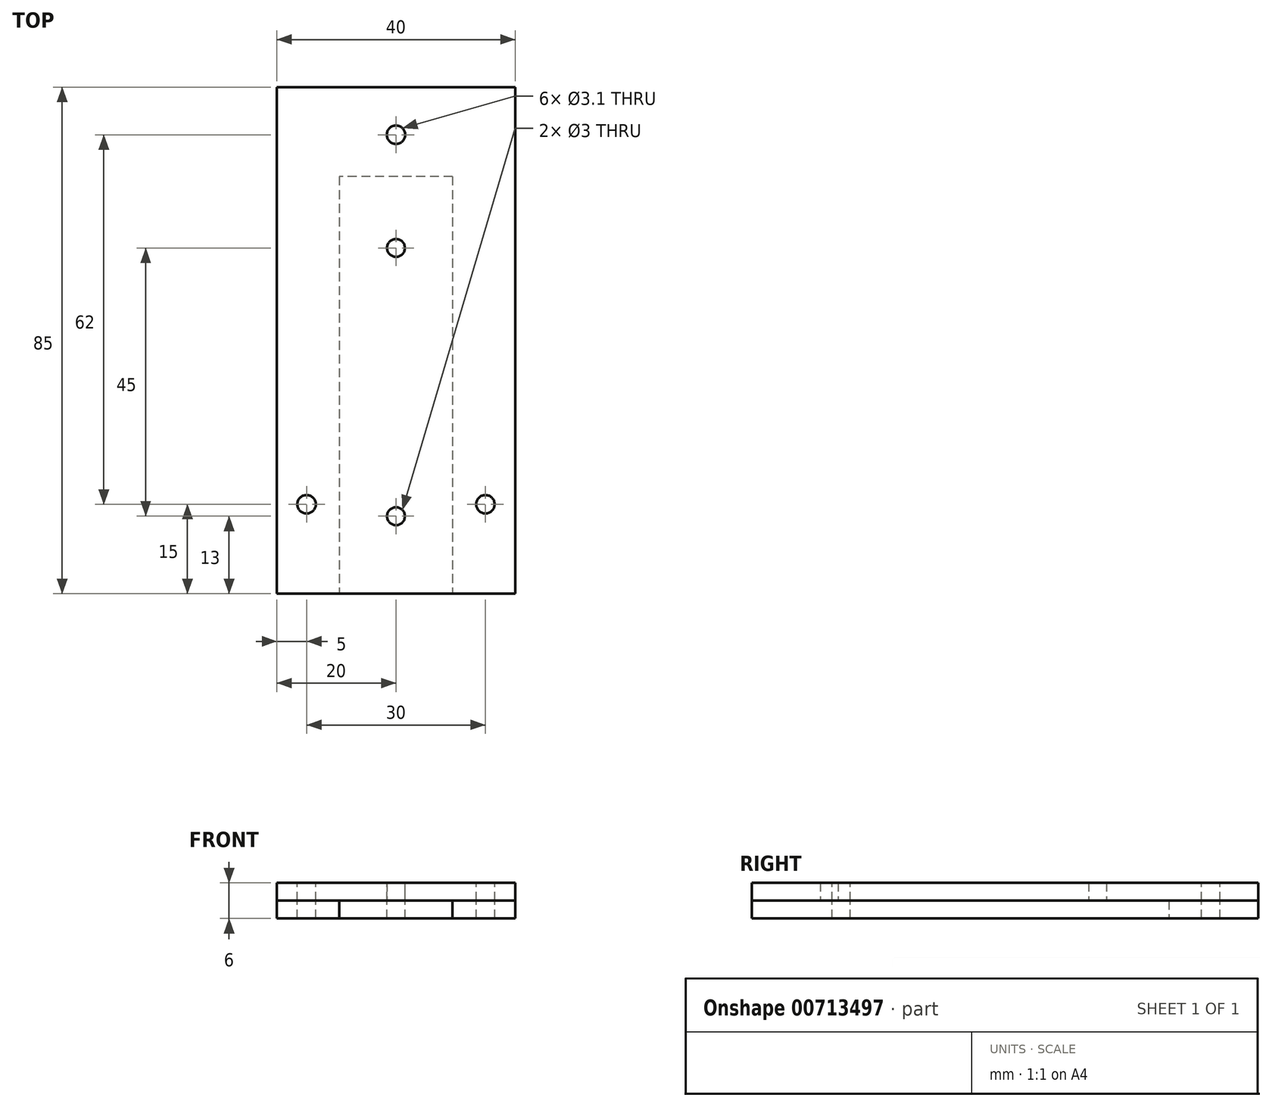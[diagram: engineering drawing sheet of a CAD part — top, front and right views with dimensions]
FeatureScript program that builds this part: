
annotation { "Feature Type Name" : "Feature", "Feature Type Description" : "" }
export const myFeature = defineFeature(function(context is Context, id is Id, definition is map)
    precondition{}
    {
        {
            var Q0;
            Q0=qCreatedBy(makeId("Top.planeOp"),FACE);
            var sketch = newSketch(context, id + "F0", { "sketchPlane" : qUnion([Q0])});
            skLineSegment(sketch, "E0.bottom", {"start": v(9.5, 35) * mm, "end": v(-9.5, 35) * mm});
            skLineSegment(sketch, "E0.top", {"start": v(9.5, -35) * mm, "end": v(-9.5, -35) * mm});
            skLineSegment(sketch, "E0.left", {"start": v(9.5, 35) * mm, "end": v(9.5, -35) * mm});
            skLineSegment(sketch, "E0.right", {"start": v(-9.5, 35) * mm, "end": v(-9.5, -35) * mm});
            skPoint(sketch, "E0.middle", {"position": v(0, 0) * mm});
            skLineSegment(sketch, "E1.bottom", {"start": v(20, 50) * mm, "end": v(-20, 50) * mm});
            skLineSegment(sketch, "E1.top", {"start": v(20, -50) * mm, "end": v(-20, -50) * mm});
            skLineSegment(sketch, "E1.left", {"start": v(20, 50) * mm, "end": v(20, -50) * mm});
            skLineSegment(sketch, "E1.right", {"start": v(-20, 50) * mm, "end": v(-20, -50) * mm});
            skLineSegment(sketch, "E2", {"start": v(-20, -35) * mm, "end": v(21.12, -35) * mm});
            skSolve(sketch);
        }
        {
            var Q0;
            Q0=makeQuery(id+"F0.imprint","IMPRINT",FACE,{"disambiguationData":[TD([[makeQuery(id+"F0.imprint","IMPRINT",EDGE,{"derivedFrom":sQuery(id+"F0.wireOp",EDGE,"E0.bottom")}),-1.0]])]});
            extrude(context, id + "F1", {"entities" : qUnion([Q0]), "depth" : 3 * mm, "offsetDistance" : 25 * mm});
        }
        {
            var Q0;
            Q0=makeQuery(id+"F1.opExtrude","CAP_FACE",FACE,{"disambiguationData":[OSD([sQuery(id+"F0.wireOp",EDGE,"E0.bottom"),sQuery(id+"F0.wireOp",EDGE,"E0.left"),sQuery(id+"F0.wireOp",EDGE,"E0.right"),sQuery(id+"F0.wireOp",EDGE,"E1.bottom"),sQuery(id+"F0.wireOp",EDGE,"E1.left"),sQuery(id+"F0.wireOp",EDGE,"E1.right"),sQuery(id+"F0.wireOp",EDGE,"E2")])],"isStart":false});
            var sketch = newSketch(context, id + "F2", { "sketchPlane" : qUnion([Q0])});
            skLineSegment(sketch, "E3.bottom", {"start": v(20, 50) * mm, "end": v(-20, 50) * mm});
            skLineSegment(sketch, "E3.top", {"start": v(20, -50) * mm, "end": v(-20, -50) * mm});
            skLineSegment(sketch, "E3.left", {"start": v(20, 50) * mm, "end": v(20, -50) * mm});
            skLineSegment(sketch, "E3.right", {"start": v(-20, 50) * mm, "end": v(-20, -50) * mm});
            skPoint(sketch, "E3.middle", {"position": v(0, 0) * mm});
            skLineSegment(sketch, "E4", {"start": v(-20, -35) * mm, "end": v(20, -35) * mm});
            skSolve(sketch);
        }
        {
            var Q0;
            {var subQ4=sQuery(id+"F2.wireOp",EDGE,"E3.bottom");Q0=makeQuery(id+"F2.imprint","IMPRINT",FACE,{"disambiguationData":[TD([[makeQuery(id+"F2.imprint","IMPRINT",EDGE,{"derivedFrom":subQ4}),1.0]])]});}
            var Q1;
            Q1=makeQuery(id+"F2.imprint","IMPRINT",FACE,{"disambiguationData":[TD([[makeQuery(id+"F2.imprint","IMPRINT",EDGE,{"derivedFrom":makeQuery(id+"F1.opExtrude","CAP_EDGE",EDGE,{"disambiguationData":[OSD([sQuery(id+"F0.wireOp",EDGE,"E0.bottom")])],"isStart":false})}),1.0]])]});
            extrude(context, id + "F3", {"entities" : qUnion([Q0, Q1]), "depth" : 3 * mm, "offsetDistance" : 25 * mm});
        }
        {
            var Q0;
            Q0=makeQuery(id+"F3.opExtrude","CAP_FACE",FACE,{"disambiguationData":[OSD([sQuery(id+"F2.wireOp",EDGE,"E3.bottom"),sQuery(id+"F2.wireOp",EDGE,"E3.left"),sQuery(id+"F2.wireOp",EDGE,"E3.right"),sQuery(id+"F2.wireOp",EDGE,"E4")])],"isStart":false});
            var sketch = newSketch(context, id + "F4", { "sketchPlane" : qUnion([Q0])});
            skCircle(sketch, "E5", {"center": v(-15, -20) * mm, "radius": 1.55 * mm});
            skCircle(sketch, "E6", {"center": v(15, -20) * mm, "radius": 1.55 * mm});
            skCircle(sketch, "E7", {"center": v(0, 42) * mm, "radius": 1.55 * mm});
            skSolve(sketch);
        }
        {
            var Q0;
            Q0 = qSketchRegion(id + "F4", true);
            extrude(context, id + "F5", {"entities" : qUnion([Q0]), "operationType" : NewBodyOperationType.REMOVE, "oppositeDirection" : true, "depth" : 25 * mm, "offsetDistance" : 25 * mm});
        }
        {
            var Q0;
            Q0=makeQuery(id+"F3.opExtrude","CAP_FACE",FACE,{"disambiguationData":[OSD([sQuery(id+"F2.wireOp",EDGE,"E3.bottom"),sQuery(id+"F2.wireOp",EDGE,"E3.left"),sQuery(id+"F2.wireOp",EDGE,"E3.right"),sQuery(id+"F2.wireOp",EDGE,"E4")])],"isStart":true});
            var sketch = newSketch(context, id + "F6", { "sketchPlane" : qUnion([Q0])});
            skCircle(sketch, "E8", {"center": v(0, -23) * mm, "radius": 1.5 * mm});
            skCircle(sketch, "E9", {"center": v(0, 22) * mm, "radius": 1.5 * mm});
            skSolve(sketch);
        }
        {
            var Q0;
            Q0 = qSketchRegion(id + "F6", true);
            extrude(context, id + "F7", {"entities" : qUnion([Q0]), "operationType" : NewBodyOperationType.REMOVE, "oppositeDirection" : true, "depth" : 25 * mm, "offsetDistance" : 25 * mm});
        }
    });
